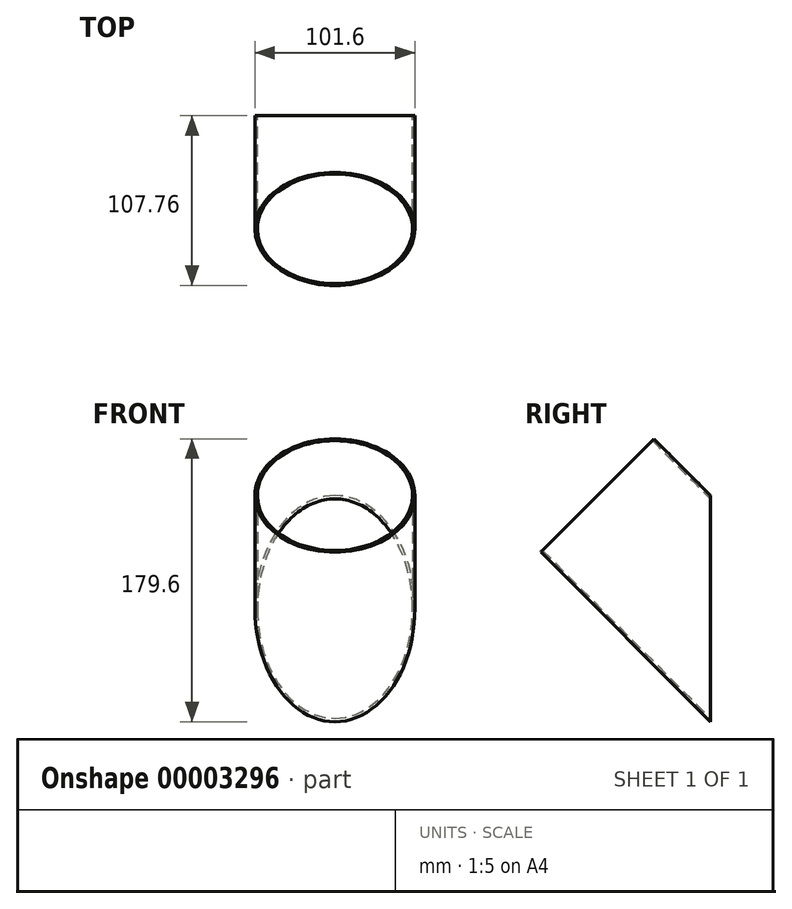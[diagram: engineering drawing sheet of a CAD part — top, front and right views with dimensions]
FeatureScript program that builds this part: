
annotation { "Feature Type Name" : "Feature", "Feature Type Description" : "" }
export const myFeature = defineFeature(function(context is Context, id is Id, definition is map)
    precondition{}
    {
        {
            var Q0;
            Q0=qCreatedBy(makeId("Front.planeOp"),FACE);
            var sketch = newSketch(context, id + "F0", { "sketchPlane" : qUnion([Q0])});
            skLineSegment(sketch, "E0", {"start": v(-50.8, 0) * mm, "end": v(50.8, 0) * mm, "construction": true});
            skSolve(sketch);
        }
        {
            var Q0;
            Q0=sQuery(id+"F0.wireOp",EDGE,"E0");
            cPlane(context, id + "F1", {"entities" : qUnion([Q0]), "cplaneType" : CPlaneType.LINE_ANGLE, "offset" : 152.4 * mm, "angle" : 315 * degree, "width" : 152.4 * mm, "height" : 152.4 * mm});
        }
        {
            var Q0;
            Q0=qCreatedBy(id+"F1.planeOp",FACE);
            var sketch = newSketch(context, id + "F2", { "sketchPlane" : qUnion([Q0])});
            skCircle(sketch, "E1", {"center": v(0, 0) * mm, "radius": 50.8 * mm});
            skCircle(sketch, "E2", {"center": v(0, 0) * mm, "radius": 49.28 * mm});
            skSolve(sketch);
        }
        {
            var Q0;
            Q0=makeQuery(id+"F2.imprint","IMPRINT",FACE,{"disambiguationData":[TD([[makeQuery(id+"F2.imprint","IMPRINT",EDGE,{"derivedFrom":sQuery(id+"F2.wireOp",EDGE,"E1")}),1.0]])]});
            extrude(context, id + "F3", {"entities" : qUnion([Q0]), "endBound" : BoundingType.SYMMETRIC, "oppositeDirection" : true, "depth" : 203.2 * mm});
        }
        {
            var Q0;
            Q0=qCreatedBy(makeId("Right.planeOp"),FACE);
            var sketch = newSketch(context, id + "F4", { "sketchPlane" : qUnion([Q0])});
            skLineSegment(sketch, "E3.bottom", {"start": v(0, 190.5) * mm, "end": v(203.2, 190.5) * mm});
            skLineSegment(sketch, "E3.top", {"start": v(0, -190.5) * mm, "end": v(203.2, -190.5) * mm});
            skLineSegment(sketch, "E3.left", {"start": v(0, 190.5) * mm, "end": v(0, -190.5) * mm});
            skLineSegment(sketch, "E3.right", {"start": v(203.2, 190.5) * mm, "end": v(203.2, -190.5) * mm});
            skSolve(sketch);
        }
        {
            var Q0;
            Q0 = qSketchRegion(id + "F4", true);
            extrude(context, id + "F5", {"entities" : qUnion([Q0]), "operationType" : NewBodyOperationType.REMOVE, "endBound" : BoundingType.SYMMETRIC, "oppositeDirection" : true, "depth" : 203.2 * mm});
        }
    });
